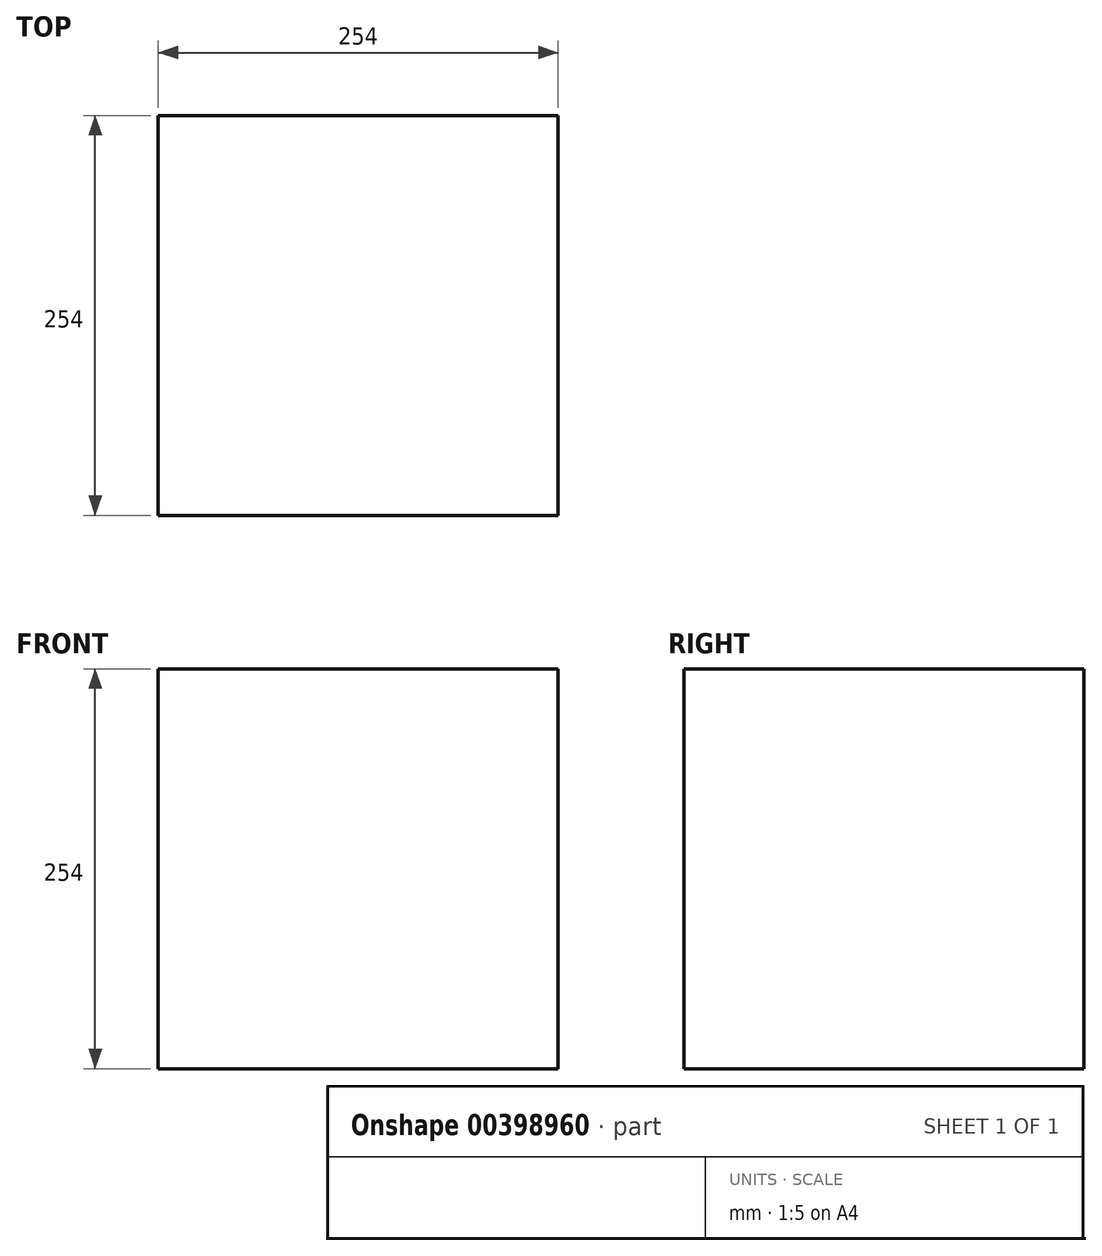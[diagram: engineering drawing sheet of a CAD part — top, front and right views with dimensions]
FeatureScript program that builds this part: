
annotation { "Feature Type Name" : "Feature", "Feature Type Description" : "" }
export const myFeature = defineFeature(function(context is Context, id is Id, definition is map)
    precondition{}
    {
        {
            var Q0;
            Q0=qCreatedBy(makeId("Top.planeOp"),FACE);
            var sketch = newSketch(context, id + "F0", { "sketchPlane" : qUnion([Q0])});
            skLineSegment(sketch, "E0.bottom", {"start": v(123.62, 127) * mm, "end": v(-130.38, 127) * mm});
            skLineSegment(sketch, "E0.top", {"start": v(123.62, -127) * mm, "end": v(-130.38, -127) * mm});
            skLineSegment(sketch, "E0.left", {"start": v(123.62, 127) * mm, "end": v(123.62, -127) * mm});
            skLineSegment(sketch, "E0.right", {"start": v(-130.38, 127) * mm, "end": v(-130.38, -127) * mm});
            skPoint(sketch, "E0.middle", {"position": v(-3.38, 0) * mm});
            skSolve(sketch);
        }
        {
            var Q0;
            Q0 = qSketchRegion(id + "F0", true);
            extrude(context, id + "F1", {"entities" : qUnion([Q0]), "depth" : 254 * mm, "symmetric" : true});
        }
    });
